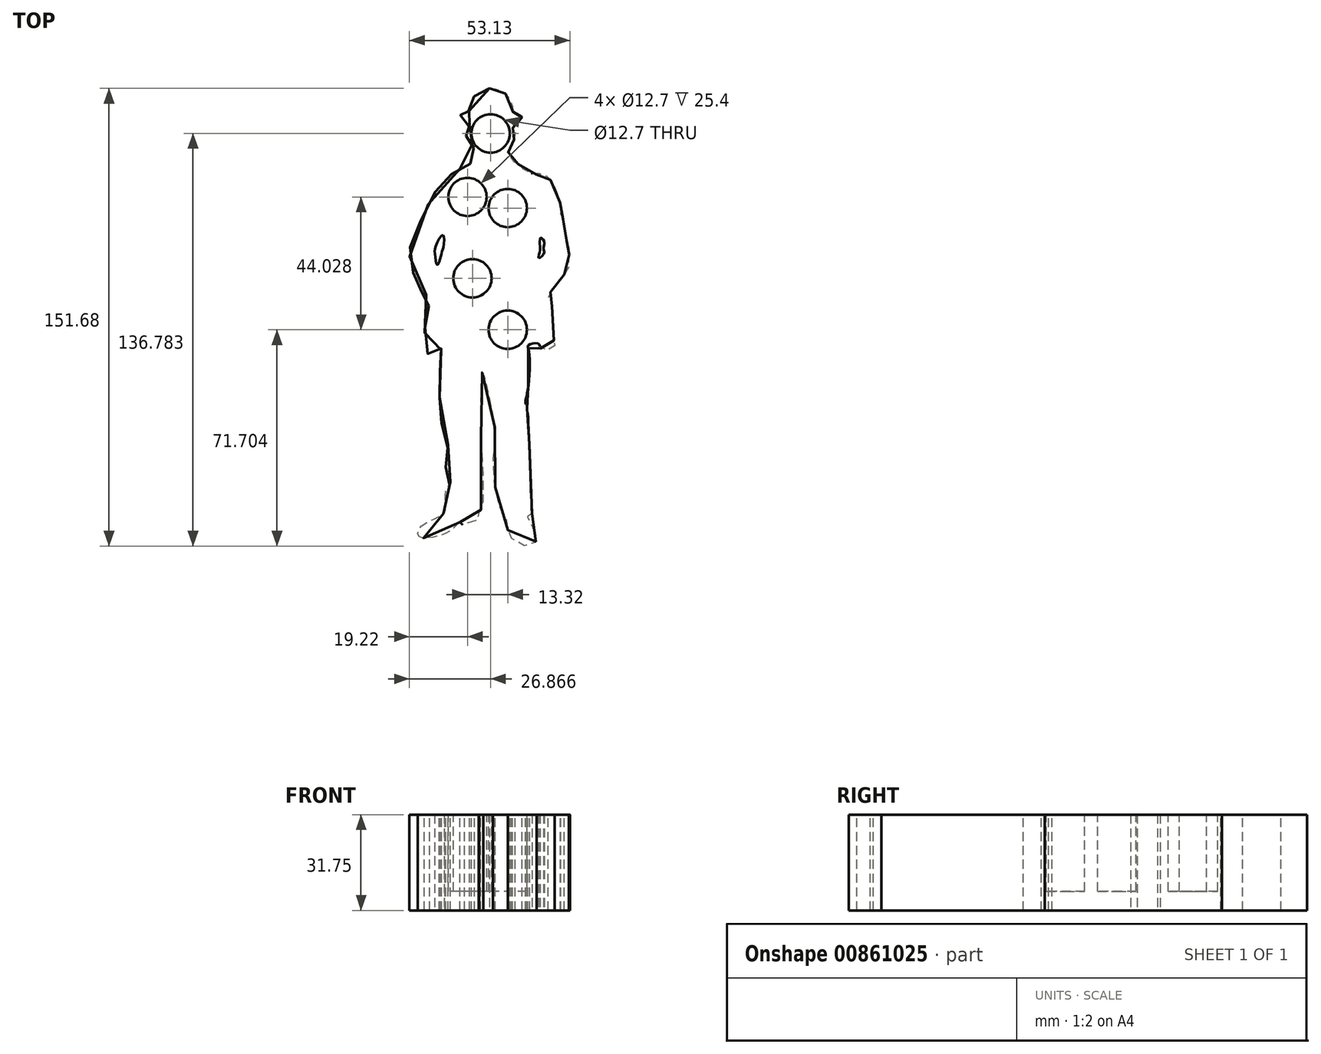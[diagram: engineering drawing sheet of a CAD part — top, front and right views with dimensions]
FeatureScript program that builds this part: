
annotation { "Feature Type Name" : "Feature", "Feature Type Description" : "" }
export const myFeature = defineFeature(function(context is Context, id is Id, definition is map)
    precondition{}
    {
        {
            var Q0;
            Q0=qCreatedBy(makeId("Top.planeOp"),FACE);
            var sketch = newSketch(context, id + "F0", { "sketchPlane" : qUnion([Q0])});
            skFitSpline(sketch, "E0", {"points": [v(-6.08, 48.55) * mm, v(-3.63, 48.34) * mm, v(-1.61, 47.49) * mm, v(0, 46) * mm, v(1.58, 42.92) * mm, v(1.8, 40.69) * mm, v(3.28, 40.37) * mm, v(4.45, 39.73) * mm, v(4.77, 39.4) * mm, v(4.56, 38.66) * mm, v(2.93, 37.4) * mm, v(1.86, 36.83) * mm, v(1.8, 35.38) * mm, v(2.36, 35.2) * mm, v(2.49, 34.12) * mm, v(2.17, 32.16) * mm, v(1.73, 31.02) * mm, v(1.16, 30.65) * mm, v(1.1, 29.32) * mm, v(0, 26.8) * mm, v(0.6, 26.35) * mm, v(1.48, 24.84) * mm, v(4.38, 22.88) * mm, v(4.76, 22.19) * mm, v(9.56, 20.04) * mm, v(10.38, 20.36) * mm, v(12.34, 19.85) * mm, v(14.48, 17.9) * mm, v(16.14, 14.5) * mm, v(17.52, 9.28) * mm, v(17.52, 6.98) * mm, v(17.98, 6.21) * mm, v(18.75, 2.84) * mm, v(18.9, 0) * mm, v(19.97, -3.15) * mm, v(20.13, -4.53) * mm, v(20.59, -5.91) * mm, v(20.13, -7.3) * mm, v(20.13, -10.51) * mm, v(17.98, -14.04) * mm, v(16.3, -16.2) * mm, v(13.68, -19.57) * mm, v(13.37, -20.34) * mm, v(14.14, -21.57) * mm, v(14.76, -24.94) * mm, v(15.22, -34.61) * mm, v(15.06, -37.68) * mm, v(11.07, -37.83) * mm, v(10.3, -36.15) * mm, v(6.93, -36.45) * mm, v(7.07, -38.77) * mm, v(6.6, -51.82) * mm, v(5.88, -55.38) * mm, v(6.36, -57.52) * mm, v(6.83, -62.5) * mm, v(8.02, -92.4) * mm], "startDerivative": vector(140.76, -3.2) * mm, "endDerivative": vector(22.08, -581.17) * mm});
            skFitSpline(sketch, "E1", {"points": [v(8.02, -92.4) * mm, v(6.48, -92.4) * mm, v(8.02, -96.53) * mm, v(9.41, -101.3) * mm, v(6.48, -103.13) * mm, v(1.36, -100.56) * mm, v(0, -97.63) * mm, v(0, -95.25) * mm, v(-1.76, -92.4) * mm, v(-4.87, -76.02) * mm, v(-4.14, -67.42) * mm, v(-6.34, -52.22) * mm, v(-8.35, -45.44) * mm, v(-8.9, -56.43) * mm, v(-8.53, -73.28) * mm, v(-8.72, -90.86) * mm, v(-9.63, -92.4) * mm, v(-9.63, -93.97) * mm, v(-14.94, -95.98) * mm, v(-15.86, -95.07) * mm, v(-18.42, -97.63) * mm, v(-26.11, -100.38) * mm, v(-29.41, -99.83) * mm, v(-29.04, -96.9) * mm, v(-21.35, -92.4) * mm, v(-20.62, -89.2) * mm, v(-20.25, -84.26) * mm, v(-18.97, -82.25) * mm, v(-20.25, -78.04) * mm, v(-20.44, -74.38) * mm, v(-19.89, -68.52) * mm, v(-22.45, -60.64) * mm, v(-22.45, -52.95) * mm, v(-22.45, -44.7) * mm, v(-22.09, -38.12) * mm, v(-22.09, -37.02) * mm, v(-26.48, -39.4) * mm, v(-27.4, -31.16) * mm, v(-26.48, -25.48) * mm, v(-26.11, -20.72) * mm, v(-28.31, -19.07) * mm, v(-30.5, -15.04) * mm, v(-32.54, -6.66) * mm, v(-30.77, 0) * mm, v(-25.2, 12.32) * mm, v(-20.9, 18.14) * mm, v(-15.33, 22.19) * mm, v(-11.79, 24.21) * mm, v(-11.03, 27.75) * mm, v(-11.79, 30.03) * mm, v(-13.05, 31.8) * mm, v(-14.32, 34.59) * mm, v(-13.3, 35.6) * mm, v(-12.8, 35.85) * mm, v(-13.05, 37.88) * mm, v(-15.84, 39.9) * mm, v(-15.33, 40.66) * mm, v(-13.56, 40.91) * mm, v(-12.55, 41.42) * mm, v(-11.53, 45.47) * mm, v(-9.76, 46.48) * mm, v(-6.08, 48.55) * mm], "startDerivative": vector(-213.93, 50.23) * mm, "endDerivative": vector(252.33, 162.42) * mm});
            skFitSpline(sketch, "E2", {"points": [v(-21.44, 0) * mm, v(-21.29, -3.93) * mm, v(-21.9, -5.9) * mm, v(-22.66, -8.95) * mm, v(-23.42, -9.86) * mm, v(-24.03, -6.67) * mm, v(-23.87, -3.78) * mm, v(-21.44, 0) * mm]});
            skFitSpline(sketch, "E3", {"points": [v(10.27, -7.61) * mm, v(12.1, -5.93) * mm, v(11.82, -4.52) * mm, v(12.17, -2.62) * mm, v(10.97, -0.94) * mm, v(10.62, -3.11) * mm, v(10.62, -5.43) * mm, v(10.27, -7.61) * mm]});
            skSolve(sketch);
        }
        {
            var Q0;
            Q0=makeQuery(id+"F0.imprint","IMPRINT",FACE,{"disambiguationData":[TD([[makeQuery(id+"F0.imprint","IMPRINT",EDGE,{"derivedFrom":sQuery(id+"F0.wireOp",EDGE,"E0")}),-1.0]])]});
            extrude(context, id + "F1", {"entities" : qUnion([Q0]), "depth" : 31.75 * mm, "offsetDistance" : 25.4 * mm});
        }
        {
            var Q0;
            Q0=makeQuery(id+"F1.opExtrude","CAP_FACE",FACE,{"disambiguationData":[OSD([sQuery(id+"F0.wireOp",EDGE,"E0"),sQuery(id+"F0.wireOp",EDGE,"E1"),sQuery(id+"F0.wireOp",EDGE,"E2"),sQuery(id+"F0.wireOp",EDGE,"E3")])],"isStart":false});
            var sketch = newSketch(context, id + "F2", { "sketchPlane" : qUnion([Q0])});
            skCircle(sketch, "E4", {"center": v(0, 8.92) * mm, "radius": 6.35 * mm});
            skCircle(sketch, "E5", {"center": v(-11.68, -14.37) * mm, "radius": 6.35 * mm});
            skCircle(sketch, "E6", {"center": v(-13.32, 12.6) * mm, "radius": 6.35 * mm});
            skCircle(sketch, "E7", {"center": v(0, -31.43) * mm, "radius": 6.35 * mm});
            skSolve(sketch);
        }
        {
            var Q0;
            Q0=makeQuery(id+"F2.imprint","IMPRINT",FACE,{"disambiguationData":[TD([[makeQuery(id+"F2.imprint","IMPRINT",EDGE,{"derivedFrom":sQuery(id+"F2.wireOp",EDGE,"E4")}),-1.0]])]});
            var sketch = newSketch(context, id + "F3", { "sketchPlane" : qUnion([Q0])});
            skCircle(sketch, "E8", {"center": v(-121.28, 74.15) * mm, "radius": 6.34 * mm});
            skCircle(sketch, "E9", {"center": v(-5.67, 33.65) * mm, "radius": 6.35 * mm});
            skSolve(sketch);
        }
        {
            var Q0;
            Q0 = qSketchRegion(id + "F2", true);
            extrude(context, id + "F4", {"entities" : qUnion([Q0]), "operationType" : NewBodyOperationType.REMOVE, "oppositeDirection" : true, "depth" : 25.4 * mm, "offsetDistance" : 25.4 * mm});
        }
        {
            var Q0;
            Q0 = qSketchRegion(id + "F3", true);
            extrude(context, id + "F5", {"entities" : qUnion([Q0]), "operationType" : NewBodyOperationType.REMOVE, "oppositeDirection" : true, "depth" : 50.8 * mm, "offsetDistance" : 25.4 * mm});
        }
    });
